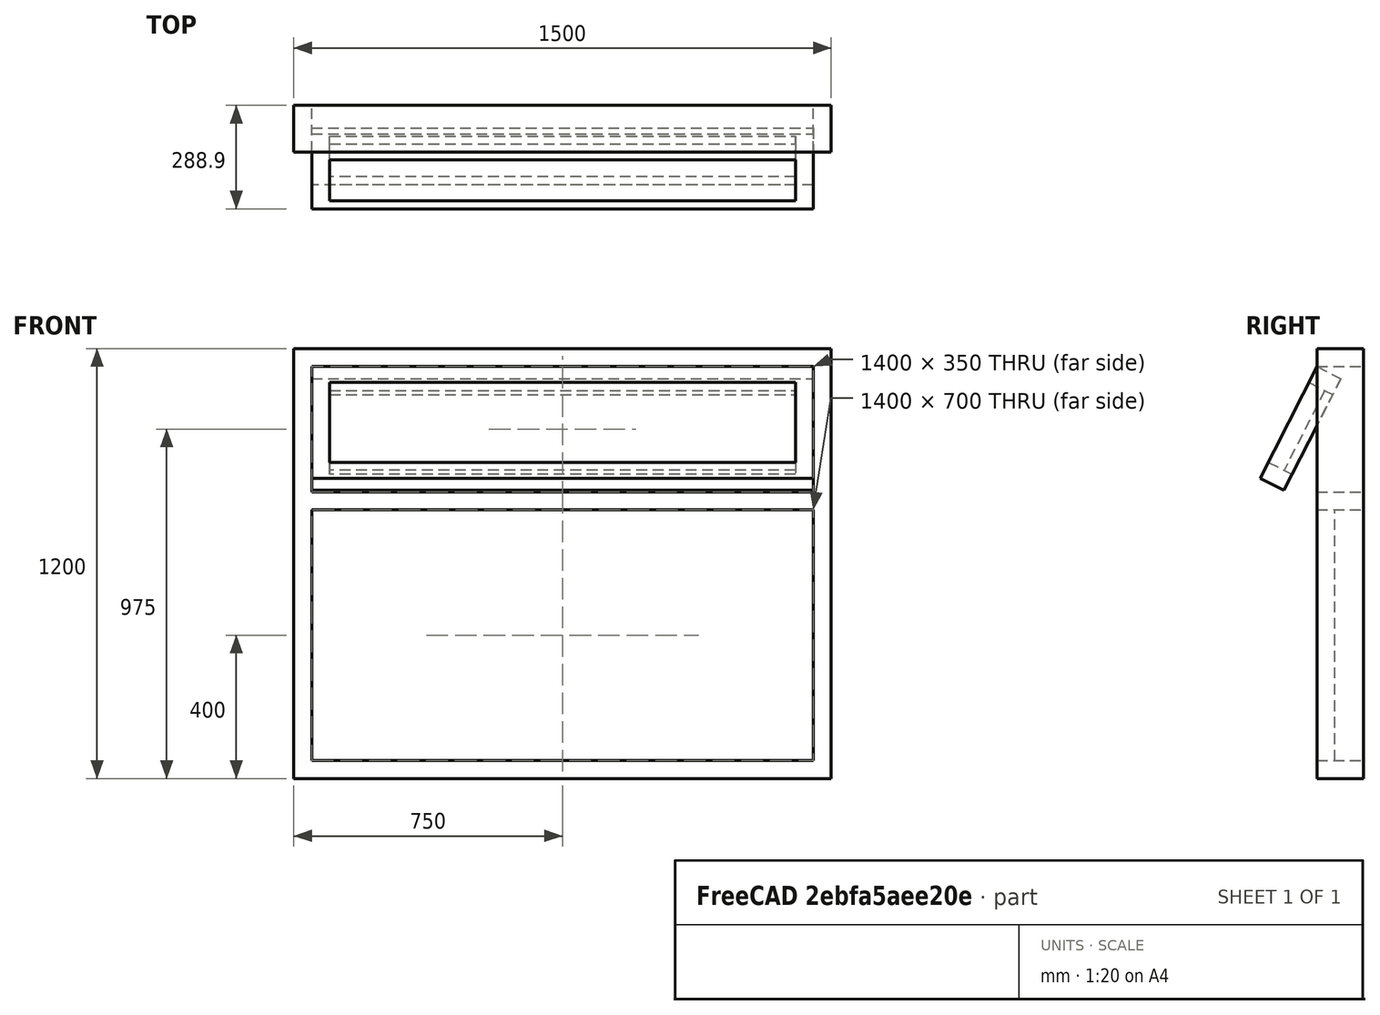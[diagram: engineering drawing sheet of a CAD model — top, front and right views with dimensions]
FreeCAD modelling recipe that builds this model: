
FCSTD DOCUMENT  (FreeCAD 0.19R23578 (Git))
Label: 2PaneTopOpen
License: Creative Commons Attribution-ShareAlike
LicenseURL: http://creativecommons.org/licenses/by-sa/4.0/
objects: Sketcher::SketchObject×1, Part::FeaturePython×1
note: 2 computed .brp shape members not serialized (recipe doc carries the construction recipe); baked Part::Feature solids carry a one-line shape summary decoded from their .brp

FEATURE [Sketcher::SketchObject] Sketch
  Placement = pos=(0,0,0) rot=(1,0,0;1.5708rad)
  expr: .Constraints.FrameOpen = .Constraints.Frame
  sketch-geometry (25):
    g0: LineSegment StartX=0 StartY=0 StartZ=0 EndX=1500 EndY=0 EndZ=0
    g1: LineSegment StartX=1500 StartY=0 StartZ=0 EndX=1500 EndY=1200 EndZ=0
    g2: LineSegment StartX=1500 StartY=1200 StartZ=0 EndX=0 EndY=1200 EndZ=0
    g3: LineSegment StartX=0 StartY=1200 StartZ=0 EndX=0 EndY=0 EndZ=0
    g4: LineSegment StartX=50 StartY=50 StartZ=0 EndX=1450 EndY=50 EndZ=0
    g5: LineSegment StartX=1450 StartY=50 StartZ=0 EndX=1450 EndY=750 EndZ=0
    g6: LineSegment StartX=1450 StartY=750 StartZ=0 EndX=50 EndY=750 EndZ=0
    g7: LineSegment StartX=50 StartY=750 StartZ=0 EndX=50 EndY=50 EndZ=0
    g8: LineSegment StartX=50 StartY=1150 StartZ=0 EndX=1450 EndY=1150 EndZ=0
    g9: LineSegment StartX=1450 StartY=1150 StartZ=0 EndX=1450 EndY=800 EndZ=0
    g10: LineSegment StartX=1450 StartY=800 StartZ=0 EndX=50 EndY=800 EndZ=0
    g11: LineSegment StartX=50 StartY=800 StartZ=0 EndX=50 EndY=1150 EndZ=0
    g12: LineSegment StartX=100 StartY=1100 StartZ=0 EndX=1400 EndY=1100 EndZ=0
    g13: LineSegment StartX=1400 StartY=1100 StartZ=0 EndX=1400 EndY=850 EndZ=0
    g14: LineSegment StartX=1400 StartY=850 StartZ=0 EndX=100 EndY=850 EndZ=0
    g15: LineSegment StartX=100 StartY=850 StartZ=0 EndX=100 EndY=1100 EndZ=0
    g16: LineSegment StartX=50 StartY=50 StartZ=0 EndX=0 EndY=50 EndZ=0
    g17: LineSegment StartX=50 StartY=50 StartZ=0 EndX=50 EndY=0 EndZ=0
    g18: LineSegment StartX=1450 StartY=1150 StartZ=0 EndX=1450 EndY=1200 EndZ=0
    g19: LineSegment StartX=1450 StartY=1150 StartZ=0 EndX=1500 EndY=1150 EndZ=0
    g20: LineSegment StartX=50 StartY=750 StartZ=0 EndX=50 EndY=800 EndZ=0
    g21: LineSegment StartX=100 StartY=1100 StartZ=0 EndX=50 EndY=1100 EndZ=0
    g22: LineSegment StartX=100 StartY=1100 StartZ=0 EndX=100 EndY=1150 EndZ=0
    g23: LineSegment StartX=1400 StartY=850 StartZ=0 EndX=1400 EndY=800 EndZ=0
    g24: LineSegment StartX=1400 StartY=850 StartZ=0 EndX=1450 EndY=850 EndZ=0
  constraints (73):
    c: Coincident(g1,g2)
    c: Coincident(g2,g3)
    c: Coincident(g3,g0)
    c: Horizontal(g0)
    c: Horizontal(g2)
    c: Vertical(g3)
    c: Coincident(g0,g-1)
    c: Coincident(g5,g6)
    c: Coincident(g6,g7)
    c: Coincident(g7,g4)
    c: Horizontal(g4)
    c: Horizontal(g6)
    c: Vertical(g7)
    c: Coincident(g9,g10)
    c: Coincident(g10,g11)
    c: Coincident(g11,g8)
    c: Horizontal(g8)
    c: Horizontal(g10)
    c: Vertical(g11)
    c: Coincident(g12,g13)
    c: Coincident(g13,g14)
    c: Coincident(g14,g15)
    c: Coincident(g15,g12)
    c: Horizontal(g12)
    c: Horizontal(g14)
    c: Vertical(g13)
    c: Vertical(g15)
    c: DistanceY(g0,g2) = 1200  'Height'
    c: DistanceY(g9,g8) = 350  'HeightTop'
    c: DistanceX(g0,g0) = 1500  'Width'
    c: Coincident(g16,g4)
    c: PointOnObject(g16,g3)
    c: Horizontal(g16)
    c: Coincident(g17,g4)
    c: PointOnObject(g17,g0)
    c: Vertical(g17)
    c: Coincident(g18,g8)
    c: PointOnObject(g18,g2)
    c: Vertical(g18)
    c: Horizontal(g19)
    c: Coincident(g20,g6)
    c: Coincident(g20,g10)
    c: Vertical(g20)
    c: Coincident(g21,g12)
    c: PointOnObject(g21,g11)
    c: Horizontal(g21)
    c: Coincident(g22,g12)
    c: PointOnObject(g22,g8)
    c: Vertical(g22)
    c: Coincident(g23,g13)
    c: PointOnObject(g23,g10)
    c: Vertical(g23)
    c: Coincident(g24,g13)
    c: PointOnObject(g24,g9)
    c: Horizontal(g24)
    c: DistanceY(g22,g22) = 50  'FrameOpen'
    c: DistanceY(g17,g17) = 50  'Frame'
    c: Equal(g16,g17)
    c: Equal(g17,g20)
    c: Equal(g20,g19)
    c: Equal(g19,g18)
    c: Equal(g24,g23)
    c: Equal(g23,g21)
    c: Equal(g21,g22)
    c: Coincident(g5,g4)
    c: Coincident(g19,g8)
    c: Coincident(g19,g9)
    c: Vertical(g5)
    c: Vertical(g9,g5)
    c: Parallel(g9,g1)
    c: PointOnObject(g19,g1)
    c: Coincident(g0,g1)
    c: Parallel(g1,g3)
FEATURE [Part::FeaturePython] Window  # Arch/BIM 170 (typed FeaturePython)
  Area = 0
  Base = -> Sketch
  Frame = 0
  Height = 0
  HoleDepth = 0
  HoleWire = 1
  HorizontalArea = 0
  IfcData = FlagForceBrep=False,FlagParametric=False,+2 more (map truncated)
  IfcType = 170
  LouvreSpacing = 0
  LouvreWidth = 0
  MoveBase = true
  MoveWithHost = true
  Normal = (0,1,0)
  Opening = 30
  OverallHeight = 0
  OverallWidth = 0
  PartitioningType = 0
  PerimeterLength = 0
  PredefinedType = 0
  Preset = 0
  SymbolElevation = false
  SymbolPlan = false
  VerticalArea = 0
  Width = 0
  WindowParts = OuterFrame | Frame | Wire1,Wire2,Wire0 | 130.0 | 0.0 | FixedGlass | Glass panel | Wire1 | 50.0 | 0.0 | TopFrame | Frame | Wire2,Wire3,Edge9,Mode2 | 75.0 | 0.0 | TopGlass | Glass panel | Wire3 | 50.0 | 0.0
  expr: OverallHeight = .Height.Value
  expr: OverallWidth = .Width.Value
